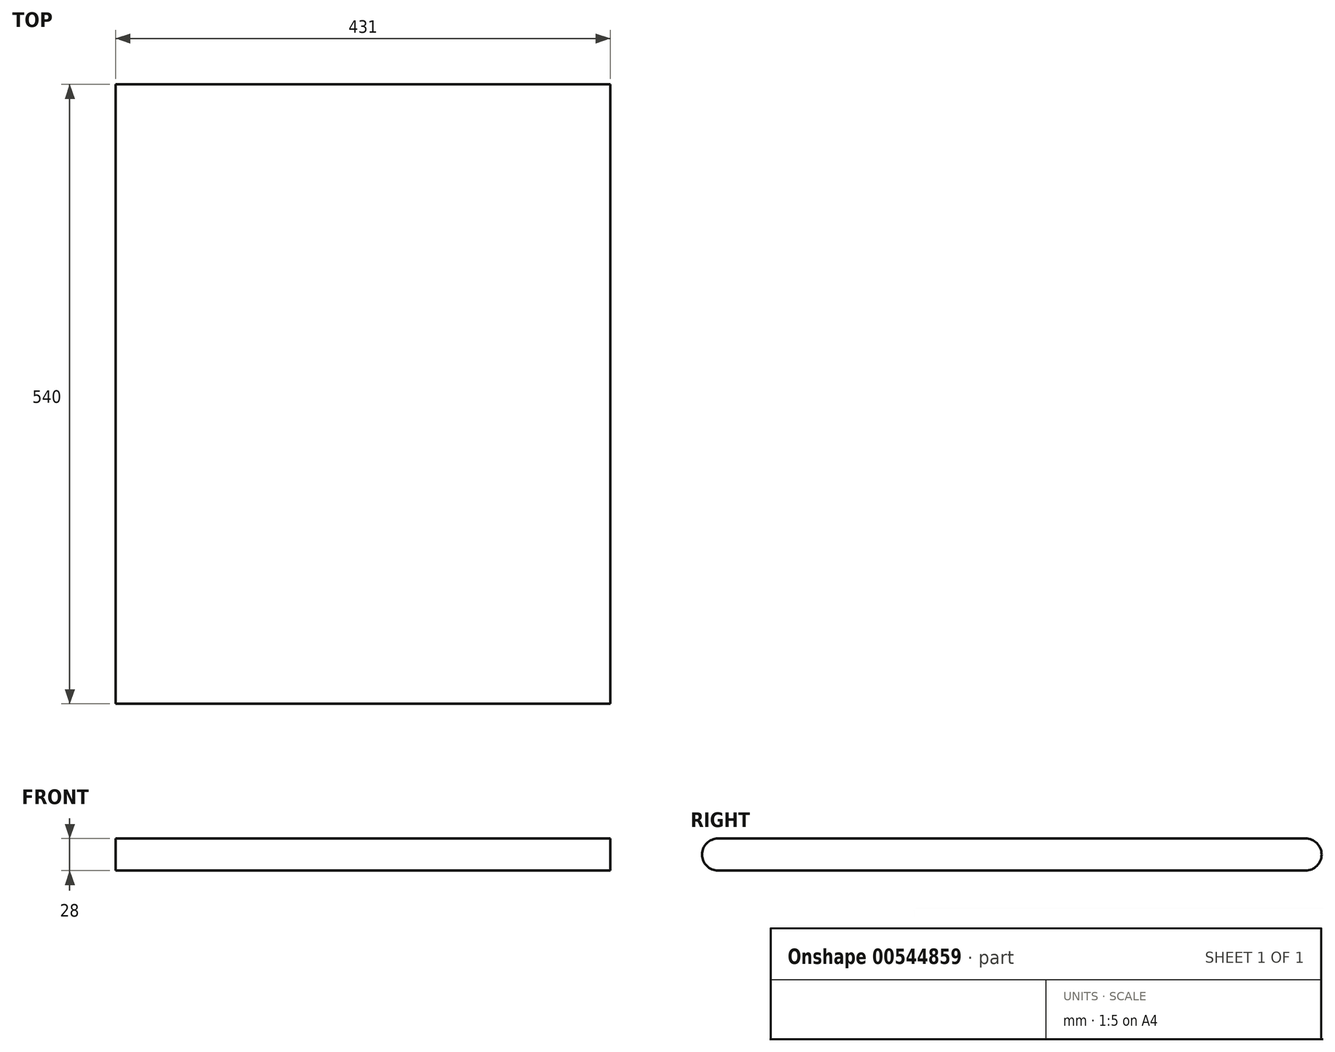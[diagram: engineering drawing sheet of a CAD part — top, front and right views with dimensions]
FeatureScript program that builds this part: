
annotation { "Feature Type Name" : "Feature", "Feature Type Description" : "" }
export const myFeature = defineFeature(function(context is Context, id is Id, definition is map)
    precondition{}
    {
        {
            var Q0;
            Q0=qCreatedBy(makeId("Right.planeOp"),FACE);
            var sketch = newSketch(context, id + "F0", { "sketchPlane" : qUnion([Q0])});
            skLineSegment(sketch, "E0.bottom", {"start": v(270, -14) * mm, "end": v(-270, -14) * mm});
            skLineSegment(sketch, "E0.top", {"start": v(270, 14) * mm, "end": v(-270, 14) * mm});
            skLineSegment(sketch, "E0.left", {"start": v(270, -14) * mm, "end": v(270, 14) * mm});
            skLineSegment(sketch, "E0.right", {"start": v(-270, -14) * mm, "end": v(-270, 14) * mm});
            skPoint(sketch, "E0.middle", {"position": v(0, 0) * mm});
            skSolve(sketch);
        }
        {
            var Q0;
            Q0 = qSketchRegion(id + "F0", true);
            extrude(context, id + "F1", {"entities" : qUnion([Q0]), "depth" : 431 * mm, "offsetDistance" : 25 * mm});
        }
        {
            var Q0;
            Q0=makeQuery(id+"F1.opExtrude","SWEPT_EDGE",EDGE,{"disambiguationData":[OSD([sQuery(id+"F0.wireOp",EDGE,"E0.top"),sQuery(id+"F0.wireOp",EDGE,"E0.left")])]});
            var Q1;
            Q1=makeQuery(id+"F1.opExtrude","SWEPT_EDGE",EDGE,{"disambiguationData":[OSD([sQuery(id+"F0.wireOp",EDGE,"E0.bottom"),sQuery(id+"F0.wireOp",EDGE,"E0.left")])]});
            var Q2;
            Q2=makeQuery(id+"F1.opExtrude","SWEPT_EDGE",EDGE,{"disambiguationData":[OSD([sQuery(id+"F0.wireOp",EDGE,"E0.top"),sQuery(id+"F0.wireOp",EDGE,"E0.right")])]});
            var Q3;
            Q3=makeQuery(id+"F1.opExtrude","SWEPT_EDGE",EDGE,{"disambiguationData":[OSD([sQuery(id+"F0.wireOp",EDGE,"E0.bottom"),sQuery(id+"F0.wireOp",EDGE,"E0.right")])]});
            fillet(context, id + "F2", {"entities" : qUnion([Q0, Q1, Q2, Q3]), "radius" : 14 * mm, "tangentPropagation" : true, "allowEdgeOverflow" : false});
        }
    });
